# Revit family: WC MIURA16
name_source: partatom
category: Aparatos sanitarios
units: mm (PartAtom-declared; Revit-internal decimal feet)

## family parameters
Compartido = Sí
Corte con vacíos al cargar = No
Cota de conector redondo = Diámetro de uso
Número OmniClass = 23.45.00.00
Punto de cálculo de habitación = No
Se basa en plano de trabajo = Sí
Siempre vertical = Sí
Tipo de pieza = Normal
Título OmniClass = Sanitary, Laundry, and Cleaning Equipment

## types (1)
- WC MIURA16
    Características del Producto = Diseño ergonómico de labio elongado, espesor de cerámica de 10 mm, sistema de descarga tipo Turbex.
    Comentarios de tipo = WC MIURA16
    Conexión de Alimentación = A la alimentacion Ø15/16-14 NS-1
    Conexión de Descarga = A la descarga se acopla al Ø de drenaje de 4" con brida sanitaria o cuello de cera.
    Descripción = W. C. Taza y Tanque MIURA Elongado, Trampa Oculta, Incluye
Asiento 4,8
    Elevación por defecto = 0.0"
    Fabricante = Helvex S.A. de C.V.
    Materials = Cerámica porcelanizada de alto brillo Grado de Calidad "A", Tipo I
    Maximum Consumption = 4,8 lpd
    Modelo = WC MIURA16
    Operation = Sistema de una descarga
    Presión Máxima de Trabajo = 85.3 psi
    Presión Mínima de Trabajo = 11.4 psi
    URL = https://helvex.com.mx
    Valves = Valv. de admisión y descarga certificadas, Valv. de admisión silenciosa, válvulas armadas y calibradas, válvula de descarga con sello hermético

## geometry (parser evidence)
native form markers: Sweep x3
no freeform markers — native parametric forms only
